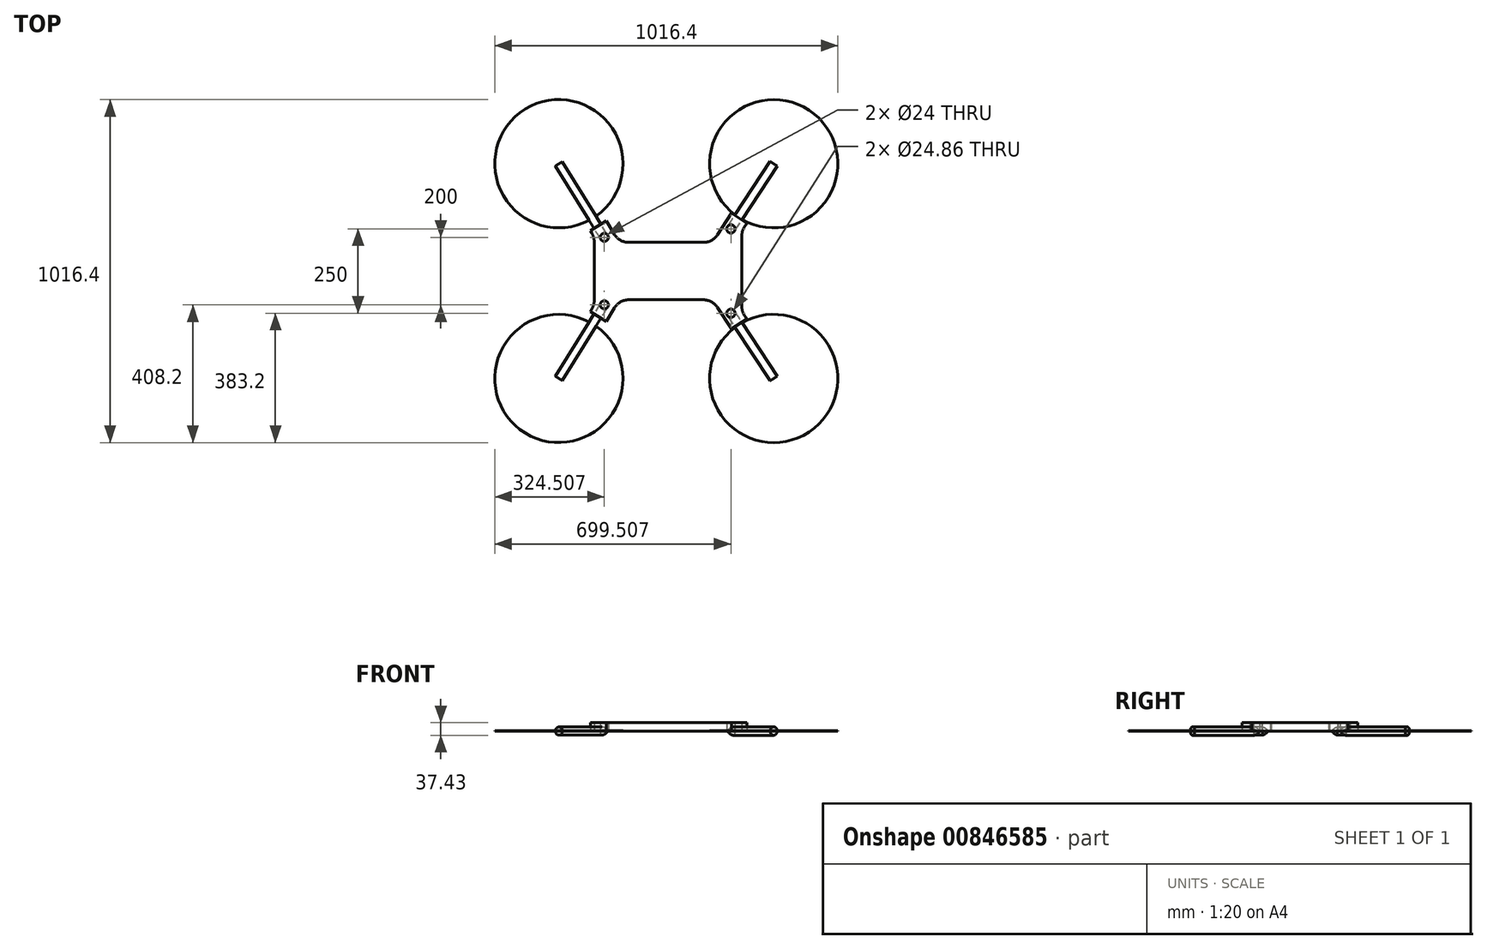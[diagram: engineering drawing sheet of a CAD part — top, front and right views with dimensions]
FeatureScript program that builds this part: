
annotation { "Feature Type Name" : "Feature", "Feature Type Description" : "" }
export const myFeature = defineFeature(function(context is Context, id is Id, definition is map)
    precondition{}
    {
        {
            var Q0;
            Q0=qCreatedBy(makeId("Top.planeOp"),FACE);
            var sketch = newSketch(context, id + "F0", { "sketchPlane" : qUnion([Q0])});
            skCircle(sketch, "E0", {"center": v(-318.2, 318.2) * mm, "radius": 190 * mm});
            skCircle(sketch, "E1", {"center": v(318.2, 318.2) * mm, "radius": 190 * mm});
            skCircle(sketch, "E2", {"center": v(318.2, -318.2) * mm, "radius": 190 * mm});
            skCircle(sketch, "E3", {"center": v(-318.2, -318.2) * mm, "radius": 190 * mm});
            skLineSegment(sketch, "E4.bottom", {"start": v(-318.2, 318.2) * mm, "end": v(318.2, 318.2) * mm, "construction": true});
            skLineSegment(sketch, "E4.top", {"start": v(-318.2, -318.2) * mm, "end": v(318.2, -318.2) * mm, "construction": true});
            skLineSegment(sketch, "E4.left", {"start": v(-318.2, 318.2) * mm, "end": v(-318.2, -318.2) * mm, "construction": true});
            skLineSegment(sketch, "E4.right", {"start": v(318.2, 318.2) * mm, "end": v(318.2, -318.2) * mm, "construction": true});
            skPoint(sketch, "E5", {"position": v(0, 318.2) * mm});
            skPoint(sketch, "E6", {"position": v(318.2, 0) * mm});
            skLineSegment(sketch, "E7", {"start": v(-318.2, 318.2) * mm, "end": v(-183.7, 100) * mm});
            skLineSegment(sketch, "E8", {"start": v(-183.7, 100) * mm, "end": v(-173.48, 106.3) * mm});
            skLineSegment(sketch, "E9", {"start": v(-173.48, 106.3) * mm, "end": v(-307.98, 324.5) * mm});
            skLineSegment(sketch, "E10", {"start": v(-307.98, 324.5) * mm, "end": v(-318.2, 318.2) * mm});
            skLineSegment(sketch, "E11", {"start": v(-225.2, 119.97) * mm, "end": v(-220.98, 113.13) * mm});
            skLineSegment(sketch, "E12", {"start": v(-213.54, 86.9) * mm, "end": v(-213.54, 0) * mm});
            skLineSegment(sketch, "E13", {"start": v(-225.2, 119.97) * mm, "end": v(-178.33, 148.85) * mm});
            skLineSegment(sketch, "E14", {"start": v(-178.33, 148.85) * mm, "end": v(-153.62, 108.76) * mm});
            skLineSegment(sketch, "E15", {"start": v(-111.05, 85) * mm, "end": v(0, 85) * mm});
            skPoint(sketch, "E16.visualSharp", {"position": v(-138.97, 85) * mm});
            skArc(sketch, "E16.filletArc", {"start": v(-153.62, 108.76) * mm, "mid": v(-135.43, 91.34) * mm, "end": v(-111.05, 85) * mm});
            skPoint(sketch, "E17.visualSharp", {"position": v(-213.54, 101.06) * mm});
            skArc(sketch, "E17.filletArc", {"start": v(-213.54, 86.9) * mm, "mid": v(-215.44, 100.53) * mm, "end": v(-220.98, 113.13) * mm});
            skLineSegment(sketch, "E18", {"start": v(0, 85) * mm, "end": v(109.84, 85) * mm});
            skLineSegment(sketch, "E19", {"start": v(318.2, 318.2) * mm, "end": v(191.3, 125) * mm});
            skLineSegment(sketch, "E20", {"start": v(191.3, 125) * mm, "end": v(180.92, 131.82) * mm});
            skLineSegment(sketch, "E21", {"start": v(180.92, 131.82) * mm, "end": v(307.8, 325.02) * mm});
            skLineSegment(sketch, "E22", {"start": v(307.8, 325.02) * mm, "end": v(318.2, 318.2) * mm});
            skLineSegment(sketch, "E23", {"start": v(151.63, 107.55) * mm, "end": v(193.6, 171.45) * mm});
            skLineSegment(sketch, "E24", {"start": v(193.6, 171.45) * mm, "end": v(238.32, 142.07) * mm});
            skLineSegment(sketch, "E25", {"start": v(238.32, 142.07) * mm, "end": v(232.14, 132.65) * mm});
            skLineSegment(sketch, "E26", {"start": v(223.93, 105.2) * mm, "end": v(223.93, 0) * mm});
            skPoint(sketch, "E27.visualSharp", {"position": v(136.82, 85) * mm});
            skArc(sketch, "E27.filletArc", {"start": v(109.84, 85) * mm, "mid": v(133.58, 91) * mm, "end": v(151.63, 107.55) * mm});
            skPoint(sketch, "E28.visualSharp", {"position": v(223.93, 120.15) * mm});
            skArc(sketch, "E28.filletArc", {"start": v(232.14, 132.65) * mm, "mid": v(226.02, 119.52) * mm, "end": v(223.93, 105.2) * mm});
            skLineSegment(sketch, "E29.MirrorCS", {"start": v(307.8, -325.02) * mm, "end": v(318.2, -318.2) * mm});
            skLineSegment(sketch, "E30.MirrorCS", {"start": v(-307.98, -324.5) * mm, "end": v(-318.2, -318.2) * mm});
            skArc(sketch, "E31.MirrorCS", {"start": v(-153.62, -108.76) * mm, "mid": v(-135.43, -91.34) * mm, "end": v(-111.05, -85) * mm});
            skArc(sketch, "E32.MirrorCS", {"start": v(232.14, -132.65) * mm, "mid": v(226.02, -119.52) * mm, "end": v(223.93, -105.2) * mm});
            skArc(sketch, "E33.MirrorCS", {"start": v(109.84, -85) * mm, "mid": v(133.58, -91) * mm, "end": v(151.63, -107.55) * mm});
            skLineSegment(sketch, "E34.MirrorCS", {"start": v(-225.2, -119.97) * mm, "end": v(-178.33, -148.85) * mm});
            skLineSegment(sketch, "E35.MirrorCS", {"start": v(151.63, -107.55) * mm, "end": v(193.6, -171.45) * mm});
            skLineSegment(sketch, "E36.MirrorCS", {"start": v(-183.7, -100) * mm, "end": v(-173.48, -106.3) * mm});
            skLineSegment(sketch, "E37.MirrorCS", {"start": v(193.6, -171.45) * mm, "end": v(238.32, -142.07) * mm});
            skArc(sketch, "E38.MirrorCS", {"start": v(-213.54, -86.9) * mm, "mid": v(-215.44, -100.53) * mm, "end": v(-220.98, -113.13) * mm});
            skLineSegment(sketch, "E39.MirrorCS", {"start": v(191.3, -125) * mm, "end": v(180.92, -131.82) * mm});
            skLineSegment(sketch, "E40.MirrorCS", {"start": v(223.93, -105.2) * mm, "end": v(223.93, 0) * mm});
            skLineSegment(sketch, "E41.MirrorCS", {"start": v(-178.33, -148.85) * mm, "end": v(-153.62, -108.76) * mm});
            skPoint(sketch, "E42.MirrorP", {"position": v(223.93, -120.15) * mm});
            skPoint(sketch, "E43.MirrorP", {"position": v(136.82, -85) * mm});
            skLineSegment(sketch, "E44.MirrorCS", {"start": v(238.32, -142.07) * mm, "end": v(232.14, -132.65) * mm});
            skLineSegment(sketch, "E45.MirrorCS", {"start": v(-225.2, -119.97) * mm, "end": v(-220.98, -113.13) * mm});
            skPoint(sketch, "E46.MirrorP", {"position": v(-138.97, -85) * mm});
            skPoint(sketch, "E47.MirrorP", {"position": v(0, -318.2) * mm});
            skLineSegment(sketch, "E48.MirrorCS", {"start": v(-213.54, -86.9) * mm, "end": v(-213.54, 0) * mm});
            skLineSegment(sketch, "E49.MirrorCS", {"start": v(-318.2, -318.2) * mm, "end": v(-183.7, -100) * mm});
            skLineSegment(sketch, "E50.MirrorCS", {"start": v(-111.05, -85) * mm, "end": v(0, -85) * mm});
            skPoint(sketch, "E51.MirrorP", {"position": v(-213.54, -101.06) * mm});
            skLineSegment(sketch, "E52.MirrorCS", {"start": v(318.2, -318.2) * mm, "end": v(191.3, -125) * mm});
            skLineSegment(sketch, "E53.MirrorCS", {"start": v(0, -85) * mm, "end": v(109.84, -85) * mm});
            skLineSegment(sketch, "E54.MirrorCS", {"start": v(-173.48, -106.3) * mm, "end": v(-307.98, -324.5) * mm});
            skLineSegment(sketch, "E55.MirrorCS", {"start": v(180.92, -131.82) * mm, "end": v(307.8, -325.02) * mm});
            skCircle(sketch, "E56", {"center": v(-183.7, 100) * mm, "radius": 12 * mm});
            skCircle(sketch, "E57", {"center": v(-183.7, -100) * mm, "radius": 12 * mm});
            skCircle(sketch, "E58", {"center": v(191.3, 125) * mm, "radius": 12.43 * mm});
            skCircle(sketch, "E59", {"center": v(191.3, -125) * mm, "radius": 12.43 * mm});
            skSolve(sketch);
        }
        {
            var Q0;
            {var subQ0=sQuery(id+"F0.wireOp",EDGE,"E10");Q0=makeQuery(id+"F0.imprint","IMPRINT",FACE,{"disambiguationData":[TD([[makeQuery(id+"F0.imprint","IMPRINT",EDGE,{"derivedFrom":subQ0}),1.0]])]});}
            var Q1;
            {var subQ0=sQuery(id+"F0.wireOp",EDGE,"E8");Q1=makeQuery(id+"F0.imprint","IMPRINT",FACE,{"disambiguationData":[TD([[makeQuery(id+"F0.imprint","IMPRINT",EDGE,{"derivedFrom":subQ0}),1.0]])]});}
            var Q2;
            {var subQ0=sQuery(id+"F0.wireOp",EDGE,"E13");var subQ1=sQuery(id+"F0.wireOp",EDGE,"E7");var subQ2=makeQuery(id+"F0.imprint","INTERSECT",VERTEX,{"derivedFrom":[subQ1,subQ0]});Q2=makeQuery(id+"F0.imprint","IMPRINT",FACE,{"disambiguationData":[TD([[makeQuery(id+"F0.imprint","IMPRINT",EDGE,{"disambiguationData":[TD([[subQ2,-1.0]])],"derivedFrom":subQ1}),1.0]])]});}
            var Q3;
            {var subQ0=sQuery(id+"F0.wireOp",EDGE,"E7");var subQ1=sQuery(id+"F0.wireOp",EDGE,"E0");var subQ2=makeQuery(id+"F0.imprint","INTERSECT",VERTEX,{"derivedFrom":[subQ1,subQ0]});Q3=makeQuery(id+"F0.imprint","IMPRINT",FACE,{"disambiguationData":[TD([[makeQuery(id+"F0.imprint","IMPRINT",EDGE,{"disambiguationData":[TD([[subQ2,-1.0]])],"derivedFrom":subQ1}),-1.0]])]});}
            var Q4;
            Q4=sQuery(id+"F0.wireOp",EDGE,"E7");
            revolve(context, id + "F1", {"surfaceOperationType" : NewSurfaceOperationType.NEW, "entities" : qUnion([Q0, Q1, Q2, Q3]), "axis" : qUnion([Q4]), "revolveType" : RevolveType.FULL});
        }
        {
            var Q0;
            {var subQ0=sQuery(id+"F0.wireOp",EDGE,"E22");Q0=makeQuery(id+"F0.imprint","IMPRINT",FACE,{"disambiguationData":[TD([[makeQuery(id+"F0.imprint","IMPRINT",EDGE,{"derivedFrom":subQ0}),-1.0]])]});}
            var Q1;
            {var subQ0=sQuery(id+"F0.wireOp",EDGE,"E20");Q1=makeQuery(id+"F0.imprint","IMPRINT",FACE,{"disambiguationData":[TD([[makeQuery(id+"F0.imprint","IMPRINT",EDGE,{"derivedFrom":subQ0}),-1.0]])]});}
            var Q2;
            {var subQ0=sQuery(id+"F0.wireOp",EDGE,"E24");var subQ1=sQuery(id+"F0.wireOp",EDGE,"E19");var subQ2=makeQuery(id+"F0.imprint","INTERSECT",VERTEX,{"derivedFrom":[subQ1,subQ0]});Q2=makeQuery(id+"F0.imprint","IMPRINT",FACE,{"disambiguationData":[TD([[makeQuery(id+"F0.imprint","IMPRINT",EDGE,{"disambiguationData":[TD([[subQ2,-1.0]])],"derivedFrom":subQ1}),-1.0]])]});}
            var Q3;
            {var subQ0=sQuery(id+"F0.wireOp",EDGE,"E19");var subQ1=sQuery(id+"F0.wireOp",EDGE,"E1");var subQ2=makeQuery(id+"F0.imprint","INTERSECT",VERTEX,{"derivedFrom":[subQ1,subQ0]});Q3=makeQuery(id+"F0.imprint","IMPRINT",FACE,{"disambiguationData":[TD([[makeQuery(id+"F0.imprint","IMPRINT",EDGE,{"disambiguationData":[TD([[subQ2,1.0]])],"derivedFrom":subQ1}),-1.0]])]});}
            var Q4;
            Q4=sQuery(id+"F0.wireOp",EDGE,"E19");
            revolve(context, id + "F2", {"surfaceOperationType" : NewSurfaceOperationType.NEW, "entities" : qUnion([Q0, Q1, Q2, Q3]), "axis" : qUnion([Q4]), "revolveType" : RevolveType.FULL});
        }
        {
            var Q0;
            {var subQ0=sQuery(id+"F0.wireOp",EDGE,"E30.MirrorCS");Q0=makeQuery(id+"F0.imprint","IMPRINT",FACE,{"disambiguationData":[TD([[makeQuery(id+"F0.imprint","IMPRINT",EDGE,{"derivedFrom":subQ0}),-1.0]])]});}
            var Q1;
            {var subQ5=sQuery(id+"F0.wireOp",EDGE,"E36.MirrorCS");Q1=makeQuery(id+"F0.imprint","IMPRINT",FACE,{"disambiguationData":[TD([[makeQuery(id+"F0.imprint","IMPRINT",EDGE,{"derivedFrom":subQ5}),-1.0]])]});}
            var Q2;
            {var subQ0=sQuery(id+"F0.wireOp",EDGE,"E49.MirrorCS");var subQ1=sQuery(id+"F0.wireOp",EDGE,"E34.MirrorCS");var subQ2=makeQuery(id+"F0.imprint","INTERSECT",VERTEX,{"derivedFrom":[subQ1,subQ0]});Q2=makeQuery(id+"F0.imprint","IMPRINT",FACE,{"disambiguationData":[TD([[makeQuery(id+"F0.imprint","IMPRINT",EDGE,{"disambiguationData":[TD([[subQ2,-1.0]])],"derivedFrom":subQ1}),1.0]])]});}
            var Q3;
            {var subQ0=sQuery(id+"F0.wireOp",EDGE,"E49.MirrorCS");var subQ1=sQuery(id+"F0.wireOp",EDGE,"E3");var subQ2=makeQuery(id+"F0.imprint","INTERSECT",VERTEX,{"derivedFrom":[subQ1,subQ0]});Q3=makeQuery(id+"F0.imprint","IMPRINT",FACE,{"disambiguationData":[TD([[makeQuery(id+"F0.imprint","IMPRINT",EDGE,{"disambiguationData":[TD([[subQ2,1.0]])],"derivedFrom":subQ1}),-1.0]])]});}
            var Q4;
            Q4=sQuery(id+"F0.wireOp",EDGE,"E49.MirrorCS");
            revolve(context, id + "F3", {"surfaceOperationType" : NewSurfaceOperationType.NEW, "entities" : qUnion([Q0, Q1, Q2, Q3]), "axis" : qUnion([Q4]), "revolveType" : RevolveType.FULL});
        }
        {
            var Q0;
            {var subQ0=sQuery(id+"F0.wireOp",EDGE,"E29.MirrorCS");Q0=makeQuery(id+"F0.imprint","IMPRINT",FACE,{"disambiguationData":[TD([[makeQuery(id+"F0.imprint","IMPRINT",EDGE,{"derivedFrom":subQ0}),1.0]])]});}
            var Q1;
            {var subQ5=sQuery(id+"F0.wireOp",EDGE,"E39.MirrorCS");Q1=makeQuery(id+"F0.imprint","IMPRINT",FACE,{"disambiguationData":[TD([[makeQuery(id+"F0.imprint","IMPRINT",EDGE,{"derivedFrom":subQ5}),1.0]])]});}
            var Q2;
            {var subQ0=sQuery(id+"F0.wireOp",EDGE,"E55.MirrorCS");var subQ1=sQuery(id+"F0.wireOp",EDGE,"E37.MirrorCS");var subQ2=makeQuery(id+"F0.imprint","INTERSECT",VERTEX,{"derivedFrom":[subQ1,subQ0]});Q2=makeQuery(id+"F0.imprint","IMPRINT",FACE,{"disambiguationData":[TD([[makeQuery(id+"F0.imprint","IMPRINT",EDGE,{"disambiguationData":[TD([[subQ2,-1.0]])],"derivedFrom":subQ1}),1.0]])]});}
            var Q3;
            {var subQ0=sQuery(id+"F0.wireOp",EDGE,"E52.MirrorCS");var subQ1=sQuery(id+"F0.wireOp",EDGE,"E2");var subQ2=makeQuery(id+"F0.imprint","INTERSECT",VERTEX,{"derivedFrom":[subQ1,subQ0]});Q3=makeQuery(id+"F0.imprint","IMPRINT",FACE,{"disambiguationData":[TD([[makeQuery(id+"F0.imprint","IMPRINT",EDGE,{"disambiguationData":[TD([[subQ2,-1.0]])],"derivedFrom":subQ1}),-1.0]])]});}
            var Q4;
            Q4=sQuery(id+"F0.wireOp",EDGE,"E52.MirrorCS");
            revolve(context, id + "F4", {"surfaceOperationType" : NewSurfaceOperationType.NEW, "entities" : qUnion([Q0, Q1, Q2, Q3]), "axis" : qUnion([Q4]), "revolveType" : RevolveType.FULL});
        }
        {
            var Q0;
            {var subQ15=sQuery(id+"F0.wireOp",EDGE,"E11");Q0=makeQuery(id+"F0.imprint","IMPRINT",FACE,{"disambiguationData":[TD([[makeQuery(id+"F0.imprint","IMPRINT",EDGE,{"derivedFrom":subQ15}),1.0]])]});}
            var Q1;
            {var subQ0=sQuery(id+"F0.wireOp",EDGE,"E24");var subQ1=sQuery(id+"F0.wireOp",EDGE,"E19");var subQ2=makeQuery(id+"F0.imprint","INTERSECT",VERTEX,{"derivedFrom":[subQ1,subQ0]});Q1=makeQuery(id+"F0.imprint","IMPRINT",FACE,{"disambiguationData":[TD([[makeQuery(id+"F0.imprint","IMPRINT",EDGE,{"disambiguationData":[TD([[subQ2,-1.0]])],"derivedFrom":subQ1}),-1.0]])]});}
            var Q2;
            {var subQ0=sQuery(id+"F0.wireOp",EDGE,"E13");var subQ1=sQuery(id+"F0.wireOp",EDGE,"E7");var subQ2=makeQuery(id+"F0.imprint","INTERSECT",VERTEX,{"derivedFrom":[subQ1,subQ0]});Q2=makeQuery(id+"F0.imprint","IMPRINT",FACE,{"disambiguationData":[TD([[makeQuery(id+"F0.imprint","IMPRINT",EDGE,{"disambiguationData":[TD([[subQ2,-1.0]])],"derivedFrom":subQ1}),1.0]])]});}
            var Q3;
            {var subQ0=sQuery(id+"F0.wireOp",EDGE,"E49.MirrorCS");var subQ1=sQuery(id+"F0.wireOp",EDGE,"E34.MirrorCS");var subQ2=makeQuery(id+"F0.imprint","INTERSECT",VERTEX,{"derivedFrom":[subQ1,subQ0]});Q3=makeQuery(id+"F0.imprint","IMPRINT",FACE,{"disambiguationData":[TD([[makeQuery(id+"F0.imprint","IMPRINT",EDGE,{"disambiguationData":[TD([[subQ2,-1.0]])],"derivedFrom":subQ1}),1.0]])]});}
            var Q4;
            {var subQ0=sQuery(id+"F0.wireOp",EDGE,"E55.MirrorCS");var subQ1=sQuery(id+"F0.wireOp",EDGE,"E37.MirrorCS");var subQ2=makeQuery(id+"F0.imprint","INTERSECT",VERTEX,{"derivedFrom":[subQ1,subQ0]});Q4=makeQuery(id+"F0.imprint","IMPRINT",FACE,{"disambiguationData":[TD([[makeQuery(id+"F0.imprint","IMPRINT",EDGE,{"disambiguationData":[TD([[subQ2,-1.0]])],"derivedFrom":subQ1}),1.0]])]});}
            extrude(context, id + "F5", {"entities" : qUnion([Q0, Q1, Q2, Q3, Q4]), "depth" : 25 * mm, "offsetDistance" : 25 * mm});
        }
        {
            var Q0;
            {var subQ0=sQuery(id+"F0.wireOp",EDGE,"E20");Q0=makeQuery(id+"F0.imprint","IMPRINT",FACE,{"disambiguationData":[TD([[makeQuery(id+"F0.imprint","IMPRINT",EDGE,{"derivedFrom":subQ0}),-1.0]])]});}
            var Q1;
            {var subQ0=sQuery(id+"F0.wireOp",EDGE,"E20");Q1=makeQuery(id+"F0.imprint","IMPRINT",FACE,{"disambiguationData":[TD([[makeQuery(id+"F0.imprint","IMPRINT",EDGE,{"derivedFrom":subQ0}),1.0]])]});}
            var Q2;
            {var subQ0=sQuery(id+"F0.wireOp",EDGE,"E8");Q2=makeQuery(id+"F0.imprint","IMPRINT",FACE,{"disambiguationData":[TD([[makeQuery(id+"F0.imprint","IMPRINT",EDGE,{"derivedFrom":subQ0}),-1.0]])]});}
            var Q3;
            {var subQ0=sQuery(id+"F0.wireOp",EDGE,"E8");Q3=makeQuery(id+"F0.imprint","IMPRINT",FACE,{"disambiguationData":[TD([[makeQuery(id+"F0.imprint","IMPRINT",EDGE,{"derivedFrom":subQ0}),1.0]])]});}
            var Q4;
            {var subQ0=sQuery(id+"F0.wireOp",EDGE,"E36.MirrorCS");Q4=makeQuery(id+"F0.imprint","IMPRINT",FACE,{"disambiguationData":[TD([[makeQuery(id+"F0.imprint","IMPRINT",EDGE,{"derivedFrom":subQ0}),1.0]])]});}
            var Q5;
            {var subQ0=sQuery(id+"F0.wireOp",EDGE,"E36.MirrorCS");Q5=makeQuery(id+"F0.imprint","IMPRINT",FACE,{"disambiguationData":[TD([[makeQuery(id+"F0.imprint","IMPRINT",EDGE,{"derivedFrom":subQ0}),-1.0]])]});}
            var Q6;
            {var subQ0=sQuery(id+"F0.wireOp",EDGE,"E39.MirrorCS");Q6=makeQuery(id+"F0.imprint","IMPRINT",FACE,{"disambiguationData":[TD([[makeQuery(id+"F0.imprint","IMPRINT",EDGE,{"derivedFrom":subQ0}),-1.0]])]});}
            var Q7;
            {var subQ0=sQuery(id+"F0.wireOp",EDGE,"E39.MirrorCS");Q7=makeQuery(id+"F0.imprint","IMPRINT",FACE,{"disambiguationData":[TD([[makeQuery(id+"F0.imprint","IMPRINT",EDGE,{"derivedFrom":subQ0}),1.0]])]});}
            var Q8;
            Q8=sQuery(id+"F0.wireOp",EDGE,"E59");
            var Q9;
            Q9=sQuery(id+"F0.wireOp",EDGE,"E58");
            var Q10;
            Q10=sQuery(id+"F0.wireOp",EDGE,"E56");
            var Q11;
            Q11=sQuery(id+"F0.wireOp",EDGE,"E57");
            extrude(context, id + "F6", {"entities" : qUnion([Q0, Q1, Q2, Q3, Q4, Q5, Q6, Q7]), "operationType" : NewBodyOperationType.REMOVE, "surfaceEntities" : qUnion([Q8, Q9, Q10, Q11]), "endBound" : BoundingType.SYMMETRIC, "depth" : 50 * mm, "offsetDistance" : 25 * mm});
        }
        {
            var Q0;
            {var subQ5=sQuery(id+"F0.wireOp",EDGE,"E30.MirrorCS");Q0=makeQuery(id+"F0.imprint","IMPRINT",FACE,{"disambiguationData":[TD([[makeQuery(id+"F0.imprint","IMPRINT",EDGE,{"derivedFrom":subQ5}),1.0]])]});}
            var Q1;
            {var subQ5=sQuery(id+"F0.wireOp",EDGE,"E30.MirrorCS");Q1=makeQuery(id+"F0.imprint","IMPRINT",FACE,{"disambiguationData":[TD([[makeQuery(id+"F0.imprint","IMPRINT",EDGE,{"derivedFrom":subQ5}),-1.0]])]});}
            extrude(context, id + "F7", {"entities" : qUnion([Q0, Q1]), "operationType" : NewBodyOperationType.ADD, "depth" : 1 * mm, "offsetDistance" : 25 * mm});
        }
        {
            var Q0;
            {var subQ5=sQuery(id+"F0.wireOp",EDGE,"E29.MirrorCS");Q0=makeQuery(id+"F0.imprint","IMPRINT",FACE,{"disambiguationData":[TD([[makeQuery(id+"F0.imprint","IMPRINT",EDGE,{"derivedFrom":subQ5}),-1.0]])]});}
            var Q1;
            {var subQ5=sQuery(id+"F0.wireOp",EDGE,"E29.MirrorCS");Q1=makeQuery(id+"F0.imprint","IMPRINT",FACE,{"disambiguationData":[TD([[makeQuery(id+"F0.imprint","IMPRINT",EDGE,{"derivedFrom":subQ5}),1.0]])]});}
            extrude(context, id + "F8", {"entities" : qUnion([Q0, Q1]), "operationType" : NewBodyOperationType.ADD, "depth" : 1 * mm, "offsetDistance" : 25 * mm});
        }
        {
            var Q0;
            {var subQ5=sQuery(id+"F0.wireOp",EDGE,"E22");Q0=makeQuery(id+"F0.imprint","IMPRINT",FACE,{"disambiguationData":[TD([[makeQuery(id+"F0.imprint","IMPRINT",EDGE,{"derivedFrom":subQ5}),-1.0]])]});}
            var Q1;
            {var subQ5=sQuery(id+"F0.wireOp",EDGE,"E22");Q1=makeQuery(id+"F0.imprint","IMPRINT",FACE,{"disambiguationData":[TD([[makeQuery(id+"F0.imprint","IMPRINT",EDGE,{"derivedFrom":subQ5}),1.0]])]});}
            extrude(context, id + "F9", {"entities" : qUnion([Q0, Q1]), "operationType" : NewBodyOperationType.ADD, "depth" : 1 * mm, "offsetDistance" : 25 * mm});
        }
        {
            var Q0;
            {var subQ5=sQuery(id+"F0.wireOp",EDGE,"E10");Q0=makeQuery(id+"F0.imprint","IMPRINT",FACE,{"disambiguationData":[TD([[makeQuery(id+"F0.imprint","IMPRINT",EDGE,{"derivedFrom":subQ5}),-1.0]])]});}
            var Q1;
            {var subQ5=sQuery(id+"F0.wireOp",EDGE,"E10");Q1=makeQuery(id+"F0.imprint","IMPRINT",FACE,{"disambiguationData":[TD([[makeQuery(id+"F0.imprint","IMPRINT",EDGE,{"derivedFrom":subQ5}),1.0]])]});}
            extrude(context, id + "F10", {"entities" : qUnion([Q0, Q1]), "operationType" : NewBodyOperationType.ADD, "depth" : 1 * mm, "offsetDistance" : 25 * mm});
        }
    });
